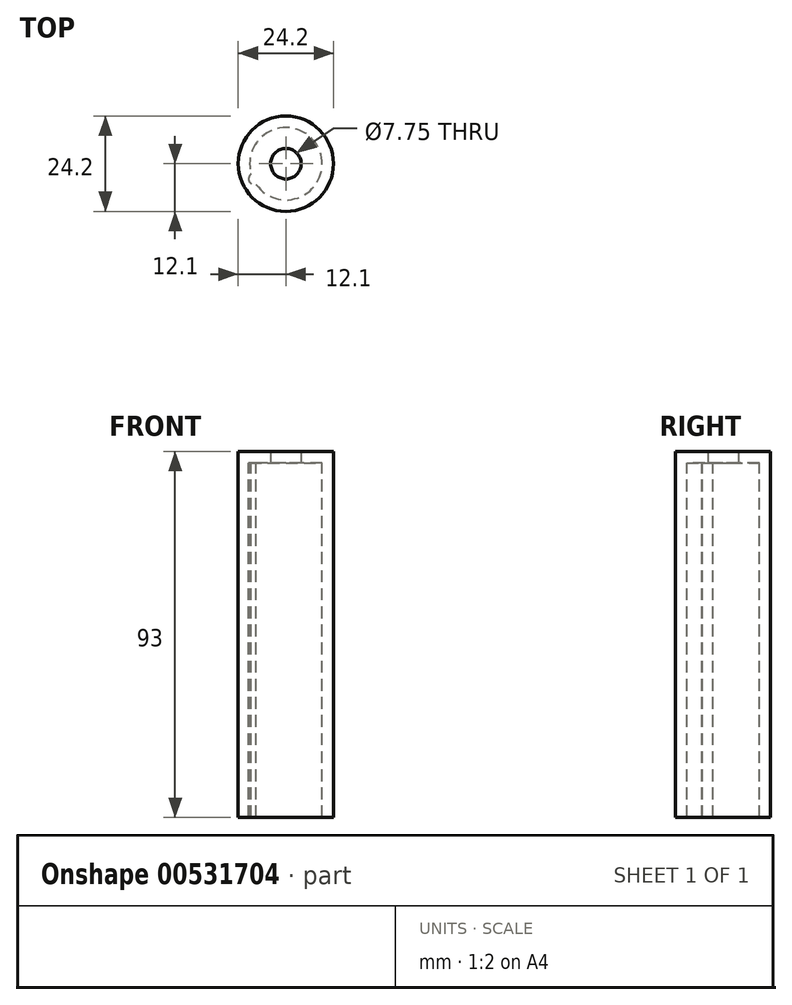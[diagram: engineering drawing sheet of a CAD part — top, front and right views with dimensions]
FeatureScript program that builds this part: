
annotation { "Feature Type Name" : "Feature", "Feature Type Description" : "" }
export const myFeature = defineFeature(function(context is Context, id is Id, definition is map)
    precondition{}
    {
        {
            var Q0;
            Q0=qCreatedBy(makeId("Top.planeOp"),FACE);
            var sketch = newSketch(context, id + "F0", { "sketchPlane" : qUnion([Q0])});
            skCircle(sketch, "E0", {"center": v(0, 0) * mm, "radius": 12.1 * mm});
            skCircle(sketch, "E1", {"center": v(0, 0) * mm, "radius": 3.88 * mm});
            skSolve(sketch);
        }
        {
            var Q0;
            Q0 = qSketchRegion(id + "F0", true);
            extrude(context, id + "F1", {"entities" : qUnion([Q0]), "depth" : 3 * mm, "offsetDistance" : 25 * mm});
        }
        {
            var Q0;
            Q0=makeQuery(id+"F1.opExtrude","CAP_FACE",FACE,{"disambiguationData":[OSD([sQuery(id+"F0.wireOp",EDGE,"E0"),sQuery(id+"F0.wireOp",EDGE,"E1")])],"isStart":true});
            var sketch = newSketch(context, id + "F2", { "sketchPlane" : qUnion([Q0])});
            skCircle(sketch, "E2", {"center": v(0, 0) * mm, "radius": 12.1 * mm});
            skArc(sketch, "E3", {"start": v(-7.53, 5.28) * mm, "mid": v(8.28, -4) * mm, "end": v(-8.82, 2.62) * mm});
            skArc(sketch, "E4", {"start": v(-7.53, 5.28) * mm, "mid": v(-9.3, 4.5) * mm, "end": v(-8.82, 2.62) * mm});
            skSolve(sketch);
        }
        {
            var Q0;
            Q0=makeQuery(id+"F2.imprint","IMPRINT",FACE,{"disambiguationData":[TD([[makeQuery(id+"F2.imprint","IMPRINT",EDGE,{"derivedFrom":sQuery(id+"F2.wireOp",EDGE,"E2")}),-1.0]])]});
            extrude(context, id + "F3", {"entities" : qUnion([Q0]), "operationType" : NewBodyOperationType.ADD, "depth" : 90 * mm, "offsetDistance" : 25 * mm});
        }
    });
